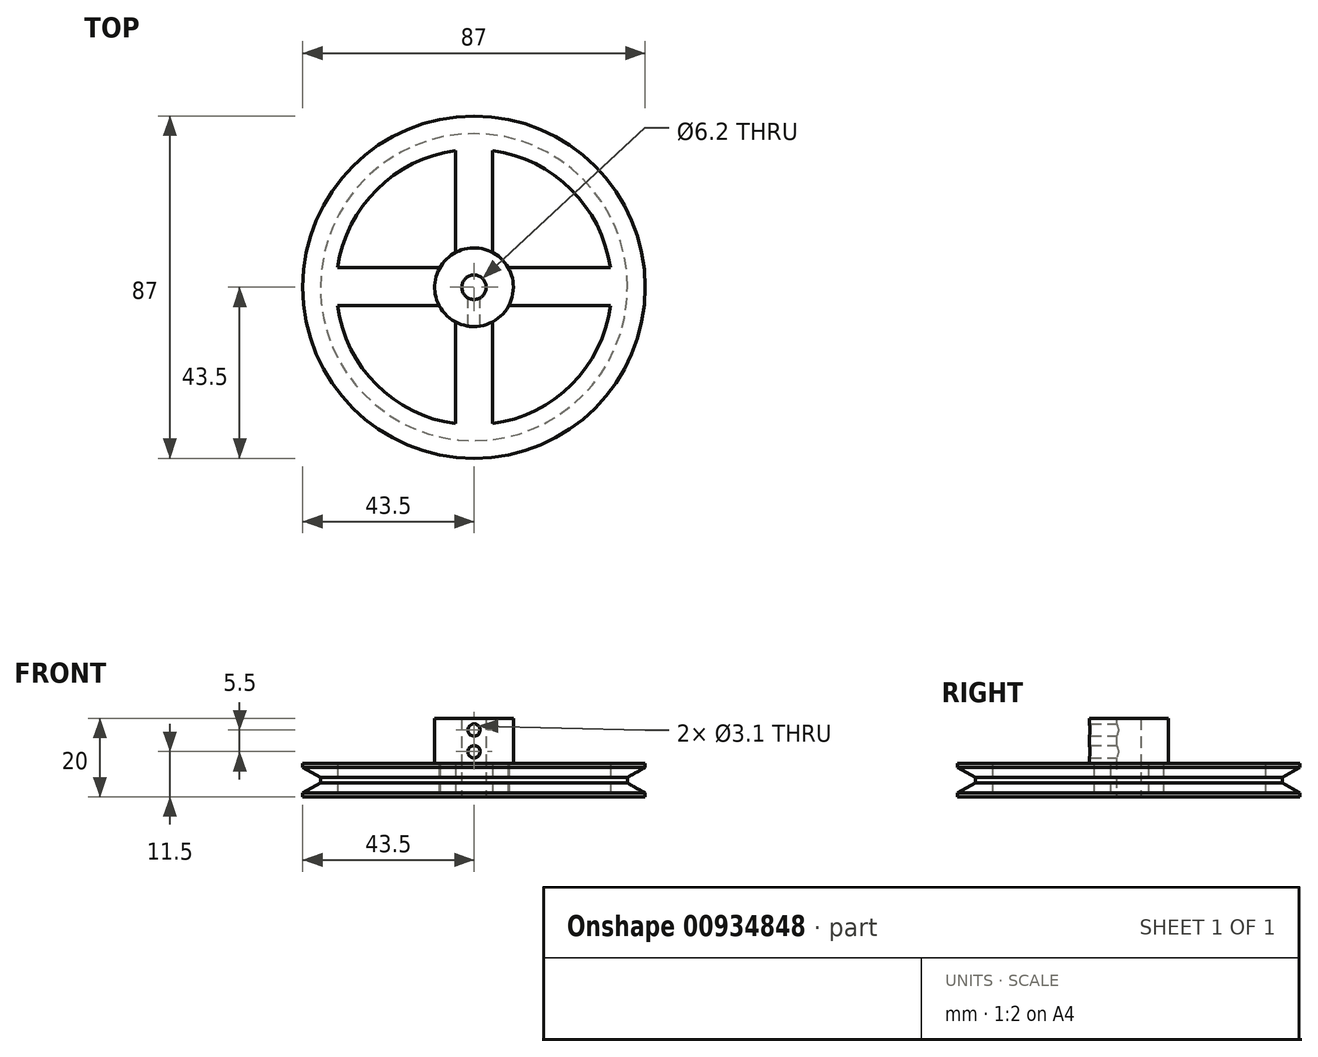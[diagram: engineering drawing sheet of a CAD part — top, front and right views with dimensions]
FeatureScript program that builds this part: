
annotation { "Feature Type Name" : "Feature", "Feature Type Description" : "" }
export const myFeature = defineFeature(function(context is Context, id is Id, definition is map)
    precondition{}
    {
        {
            var Q0;
            Q0=qCreatedBy(makeId("Top.planeOp"),FACE);
            var sketch = newSketch(context, id + "F0", { "sketchPlane" : qUnion([Q0])});
            skCircle(sketch, "E0", {"center": v(0, 0) * mm, "radius": 43.5 * mm});
            skCircle(sketch, "E1", {"center": v(0, 0) * mm, "radius": 39 * mm});
            skCircle(sketch, "E2", {"center": v(0, 0) * mm, "radius": 3.1 * mm});
            skCircle(sketch, "E3", {"center": v(0, 0) * mm, "radius": 10 * mm});
            skLineSegment(sketch, "E4", {"start": v(43.5, 0) * mm, "end": v(-43.5, 0) * mm});
            skLineSegment(sketch, "E5", {"start": v(0, 43.5) * mm, "end": v(0, -43.5) * mm});
            skLineSegment(sketch, "E6", {"start": v(-4.67, -34.69) * mm, "end": v(-4.67, -34.69) * mm});
            skLineSegment(sketch, "E7", {"start": v(4.67, -34.69) * mm, "end": v(4.67, 34.69) * mm});
            skLineSegment(sketch, "E8", {"start": v(34.69, -4.67) * mm, "end": v(-34.69, -4.67) * mm});
            skLineSegment(sketch, "E9", {"start": v(-34.64, 5) * mm, "end": v(-34.64, 5) * mm});
            skLineSegment(sketch, "E10", {"start": v(-4.67, -34.69) * mm, "end": v(-4.67, 34.69) * mm});
            skLineSegment(sketch, "E11", {"start": v(-34.69, -4.67) * mm, "end": v(-34.69, -4.67) * mm});
            skLineSegment(sketch, "E12", {"start": v(-34.64, 5) * mm, "end": v(34.64, 5) * mm});
            skArc(sketch, "E13", {"start": v(-4.67, 34.69) * mm, "mid": v(-24.75, -24.75) * mm, "end": v(34.69, -4.67) * mm});
            skArc(sketch, "E14", {"start": v(4.67, 34.69) * mm, "mid": v(0, 35) * mm, "end": v(-4.67, 34.69) * mm});
            skArc(sketch, "E15", {"start": v(34.64, 5) * mm, "mid": v(24.63, 24.87) * mm, "end": v(4.67, 34.69) * mm});
            skArc(sketch, "E16", {"start": v(34.69, -4.67) * mm, "mid": v(35, 0.17) * mm, "end": v(34.64, 5) * mm});
            skSolve(sketch);
        }
        {
            var Q0;
            Q0 = qSketchRegion(id + "F0", true);
            var Q1;
            Q1=makeQuery(id+"F0.imprint","IMPRINT",FACE,{"disambiguationData":[TD([[makeQuery(id+"F0.imprint","IMPRINT",EDGE,{"derivedFrom":sQuery(id+"F0.wireOp",EDGE,"E1")}),1.0]])]});
            var Q2;
            {var subQ2=sQuery(id+"F0.wireOp",EDGE,"Dt7iSOTS-iNF6-Fj9d-QwL8-E1cNRbcfdXUS");var subQ4=sQuery(id+"F0.wireOp",EDGE,"E1");var subQ5=makeQuery(id+"F0.imprint","INTERSECT",VERTEX,{"disambiguationData":[OD(0.0)],"derivedFrom":[subQ4,subQ2]});Q2=makeQuery(id+"F0.imprint","IMPRINT",FACE,{"disambiguationData":[TD([[makeQuery(id+"F0.imprint","IMPRINT",EDGE,{"disambiguationData":[TD([[subQ5,-1.0]])],"derivedFrom":subQ4}),1.0]])]});}
            var Q3;
            {var subQ4=sQuery(id+"F0.wireOp",EDGE,"E1");var subQ6=sQuery(id+"F0.wireOp",EDGE,"f54aecad-8b98-43cd-b3f4-bd551124e2040.MirrorCS");var subQ7=makeQuery(id+"F0.imprint","INTERSECT",VERTEX,{"disambiguationData":[OD(1.0)],"derivedFrom":[subQ4,subQ6]});Q3=makeQuery(id+"F0.imprint","IMPRINT",FACE,{"disambiguationData":[TD([[makeQuery(id+"F0.imprint","IMPRINT",EDGE,{"disambiguationData":[TD([[subQ7,1.0]])],"derivedFrom":subQ4}),1.0]])]});}
            var Q4;
            {var subQ5=sQuery(id+"F0.wireOp",EDGE,"E3");var subQ7=sQuery(id+"F0.wireOp",EDGE,"E5");var subQ8=makeQuery(id+"F0.imprint","INTERSECT",VERTEX,{"disambiguationData":[OD(1.0)],"derivedFrom":[subQ5,subQ7]});Q4=makeQuery(id+"F0.imprint","IMPRINT",FACE,{"disambiguationData":[TD([[makeQuery(id+"F0.imprint","IMPRINT",EDGE,{"disambiguationData":[TD([[subQ8,-1.0]])],"derivedFrom":subQ5}),-1.0]])]});}
            var Q5;
            {var subQ3=sQuery(id+"F0.wireOp",EDGE,"Dt7iSOTS-iNF6-Fj9d-QwL8-E1cNRbcfdXUS");var subQ5=sQuery(id+"F0.wireOp",EDGE,"E3");var subQ6=makeQuery(id+"F0.imprint","INTERSECT",VERTEX,{"disambiguationData":[OD(1.0)],"derivedFrom":[subQ5,subQ3]});Q5=makeQuery(id+"F0.imprint","IMPRINT",FACE,{"disambiguationData":[TD([[makeQuery(id+"F0.imprint","IMPRINT",EDGE,{"disambiguationData":[TD([[subQ6,-1.0]])],"derivedFrom":subQ5}),-1.0]])]});}
            var Q6;
            {var subQ0=sQuery(id+"F0.wireOp",EDGE,"Dt7iSOTS-iNF6-Fj9d-QwL8-E1cNRbcfdXUS");var subQ1=sQuery(id+"F0.wireOp",EDGE,"E3");var subQ2=makeQuery(id+"F0.imprint","INTERSECT",VERTEX,{"disambiguationData":[OD(1.0)],"derivedFrom":[subQ1,subQ0]});Q6=makeQuery(id+"F0.imprint","IMPRINT",FACE,{"disambiguationData":[TD([[makeQuery(id+"F0.imprint","IMPRINT",EDGE,{"disambiguationData":[TD([[subQ2,-1.0]])],"derivedFrom":subQ1}),1.0]])]});}
            var Q7;
            {var subQ0=sQuery(id+"F0.wireOp",EDGE,"E5");var subQ1=sQuery(id+"F0.wireOp",EDGE,"E3");var subQ2=makeQuery(id+"F0.imprint","INTERSECT",VERTEX,{"disambiguationData":[OD(1.0)],"derivedFrom":[subQ1,subQ0]});Q7=makeQuery(id+"F0.imprint","IMPRINT",FACE,{"disambiguationData":[TD([[makeQuery(id+"F0.imprint","IMPRINT",EDGE,{"disambiguationData":[TD([[subQ2,-1.0]])],"derivedFrom":subQ1}),1.0]])]});}
            var Q8;
            {var subQ0=sQuery(id+"F0.wireOp",EDGE,"E5");var subQ1=sQuery(id+"F0.wireOp",EDGE,"E2");var subQ2=makeQuery(id+"F0.imprint","INTERSECT",VERTEX,{"disambiguationData":[OD(1.0)],"derivedFrom":[subQ1,subQ0]});Q8=makeQuery(id+"F0.imprint","IMPRINT",FACE,{"disambiguationData":[TD([[makeQuery(id+"F0.imprint","IMPRINT",EDGE,{"disambiguationData":[TD([[subQ2,-1.0]])],"derivedFrom":subQ1}),-1.0]])]});}
            var Q9;
            {var subQ0=sQuery(id+"F0.wireOp",EDGE,"Dt7iSOTS-iNF6-Fj9d-QwL8-E1cNRbcfdXUS");var subQ1=sQuery(id+"F0.wireOp",EDGE,"E2");var subQ2=makeQuery(id+"F0.imprint","INTERSECT",VERTEX,{"disambiguationData":[OD(1.0)],"derivedFrom":[subQ1,subQ0]});Q9=makeQuery(id+"F0.imprint","IMPRINT",FACE,{"disambiguationData":[TD([[makeQuery(id+"F0.imprint","IMPRINT",EDGE,{"disambiguationData":[TD([[subQ2,-1.0]])],"derivedFrom":subQ1}),-1.0]])]});}
            var Q10;
            {var subQ0=sQuery(id+"F0.wireOp",EDGE,"E10");var subQ1=sQuery(id+"F0.wireOp",EDGE,"E3");var subQ2=makeQuery(id+"F0.imprint","INTERSECT",VERTEX,{"disambiguationData":[OD(1.0)],"derivedFrom":[subQ1,subQ0]});Q10=makeQuery(id+"F0.imprint","IMPRINT",FACE,{"disambiguationData":[TD([[makeQuery(id+"F0.imprint","IMPRINT",EDGE,{"disambiguationData":[TD([[subQ2,-1.0]])],"derivedFrom":subQ1}),1.0]])]});}
            var Q11;
            {var subQ0=sQuery(id+"F0.wireOp",EDGE,"E10");var subQ1=sQuery(id+"F0.wireOp",EDGE,"E3");var subQ2=makeQuery(id+"F0.imprint","INTERSECT",VERTEX,{"disambiguationData":[OD(1.0)],"derivedFrom":[subQ1,subQ0]});Q11=makeQuery(id+"F0.imprint","IMPRINT",FACE,{"disambiguationData":[TD([[makeQuery(id+"F0.imprint","IMPRINT",EDGE,{"disambiguationData":[TD([[subQ2,-1.0]])],"derivedFrom":subQ1}),-1.0]])]});}
            var Q12;
            {var subQ0=sQuery(id+"F0.wireOp",EDGE,"f54aecad-8b98-43cd-b3f4-bd551124e2040.MirrorCS");var subQ1=sQuery(id+"F0.wireOp",EDGE,"E3");var subQ2=makeQuery(id+"F0.imprint","INTERSECT",VERTEX,{"disambiguationData":[OD(1.0)],"derivedFrom":[subQ1,subQ0]});Q12=makeQuery(id+"F0.imprint","IMPRINT",FACE,{"disambiguationData":[TD([[makeQuery(id+"F0.imprint","IMPRINT",EDGE,{"disambiguationData":[TD([[subQ2,-1.0]])],"derivedFrom":subQ1}),-1.0]])]});}
            var Q13;
            {var subQ0=sQuery(id+"F0.wireOp",EDGE,"f54aecad-8b98-43cd-b3f4-bd551124e2040.MirrorCS");var subQ1=sQuery(id+"F0.wireOp",EDGE,"E3");var subQ2=makeQuery(id+"F0.imprint","INTERSECT",VERTEX,{"disambiguationData":[OD(1.0)],"derivedFrom":[subQ1,subQ0]});Q13=makeQuery(id+"F0.imprint","IMPRINT",FACE,{"disambiguationData":[TD([[makeQuery(id+"F0.imprint","IMPRINT",EDGE,{"disambiguationData":[TD([[subQ2,-1.0]])],"derivedFrom":subQ1}),1.0]])]});}
            var Q14;
            {var subQ0=sQuery(id+"F0.wireOp",EDGE,"f54aecad-8b98-43cd-b3f4-bd551124e2040.MirrorCS");var subQ1=sQuery(id+"F0.wireOp",EDGE,"E2");var subQ2=makeQuery(id+"F0.imprint","INTERSECT",VERTEX,{"disambiguationData":[OD(1.0)],"derivedFrom":[subQ1,subQ0]});Q14=makeQuery(id+"F0.imprint","IMPRINT",FACE,{"disambiguationData":[TD([[makeQuery(id+"F0.imprint","IMPRINT",EDGE,{"disambiguationData":[TD([[subQ2,-1.0]])],"derivedFrom":subQ1}),-1.0]])]});}
            var Q15;
            {var subQ0=sQuery(id+"F0.wireOp",EDGE,"0fc9e538-063d-4069-807a-62193617adc70.MirrorCS");var subQ1=sQuery(id+"F0.wireOp",EDGE,"E2");var subQ2=makeQuery(id+"F0.imprint","INTERSECT",VERTEX,{"disambiguationData":[OD(1.0)],"derivedFrom":[subQ1,subQ0]});Q15=makeQuery(id+"F0.imprint","IMPRINT",FACE,{"disambiguationData":[TD([[makeQuery(id+"F0.imprint","IMPRINT",EDGE,{"disambiguationData":[TD([[subQ2,-1.0]])],"derivedFrom":subQ1}),-1.0]])]});}
            var Q16;
            {var subQ0=sQuery(id+"F0.wireOp",EDGE,"E4");var subQ1=sQuery(id+"F0.wireOp",EDGE,"E2");var subQ2=makeQuery(id+"F0.imprint","INTERSECT",VERTEX,{"disambiguationData":[OD(0.0)],"derivedFrom":[subQ1,subQ0]});Q16=makeQuery(id+"F0.imprint","IMPRINT",FACE,{"disambiguationData":[TD([[makeQuery(id+"F0.imprint","IMPRINT",EDGE,{"disambiguationData":[TD([[subQ2,1.0]])],"derivedFrom":subQ1}),-1.0]])]});}
            var Q17;
            {var subQ0=sQuery(id+"F0.wireOp",EDGE,"c9230b24-fb15-4a67-97de-4f06d66d76500.MirrorCS");var subQ1=sQuery(id+"F0.wireOp",EDGE,"E2");var subQ2=makeQuery(id+"F0.imprint","INTERSECT",VERTEX,{"disambiguationData":[OD(0.0)],"derivedFrom":[subQ1,subQ0]});Q17=makeQuery(id+"F0.imprint","IMPRINT",FACE,{"disambiguationData":[TD([[makeQuery(id+"F0.imprint","IMPRINT",EDGE,{"disambiguationData":[TD([[subQ2,1.0]])],"derivedFrom":subQ1}),-1.0]])]});}
            var Q18;
            {var subQ0=sQuery(id+"F0.wireOp",EDGE,"c9230b24-fb15-4a67-97de-4f06d66d76500.MirrorCS");var subQ1=sQuery(id+"F0.wireOp",EDGE,"E2");var subQ2=makeQuery(id+"F0.imprint","INTERSECT",VERTEX,{"disambiguationData":[OD(0.0)],"derivedFrom":[subQ1,subQ0]});Q18=makeQuery(id+"F0.imprint","IMPRINT",FACE,{"disambiguationData":[TD([[makeQuery(id+"F0.imprint","IMPRINT",EDGE,{"disambiguationData":[TD([[subQ2,-1.0]])],"derivedFrom":subQ1}),-1.0]])]});}
            var Q19;
            {var subQ0=sQuery(id+"F0.wireOp",EDGE,"X2wNwJQT-B4Tv-bB2O-wKaQ-eUmFgRdWR0iJ");var subQ1=sQuery(id+"F0.wireOp",EDGE,"E2");var subQ2=makeQuery(id+"F0.imprint","INTERSECT",VERTEX,{"disambiguationData":[OD(0.0)],"derivedFrom":[subQ1,subQ0]});Q19=makeQuery(id+"F0.imprint","IMPRINT",FACE,{"disambiguationData":[TD([[makeQuery(id+"F0.imprint","IMPRINT",EDGE,{"disambiguationData":[TD([[subQ2,-1.0]])],"derivedFrom":subQ1}),-1.0]])]});}
            var Q20;
            {var subQ0=sQuery(id+"F0.wireOp",EDGE,"Dt7iSOTS-iNF6-Fj9d-QwL8-E1cNRbcfdXUS");var subQ1=sQuery(id+"F0.wireOp",EDGE,"E2");var subQ2=makeQuery(id+"F0.imprint","INTERSECT",VERTEX,{"disambiguationData":[OD(0.0)],"derivedFrom":[subQ1,subQ0]});Q20=makeQuery(id+"F0.imprint","IMPRINT",FACE,{"disambiguationData":[TD([[makeQuery(id+"F0.imprint","IMPRINT",EDGE,{"disambiguationData":[TD([[subQ2,-1.0]])],"derivedFrom":subQ1}),-1.0]])]});}
            var Q21;
            {var subQ0=sQuery(id+"F0.wireOp",EDGE,"E5");var subQ1=sQuery(id+"F0.wireOp",EDGE,"E2");var subQ2=makeQuery(id+"F0.imprint","INTERSECT",VERTEX,{"disambiguationData":[OD(0.0)],"derivedFrom":[subQ1,subQ0]});Q21=makeQuery(id+"F0.imprint","IMPRINT",FACE,{"disambiguationData":[TD([[makeQuery(id+"F0.imprint","IMPRINT",EDGE,{"disambiguationData":[TD([[subQ2,-1.0]])],"derivedFrom":subQ1}),-1.0]])]});}
            var Q22;
            {var subQ0=sQuery(id+"F0.wireOp",EDGE,"f54aecad-8b98-43cd-b3f4-bd551124e2040.MirrorCS");var subQ1=sQuery(id+"F0.wireOp",EDGE,"E2");var subQ2=makeQuery(id+"F0.imprint","INTERSECT",VERTEX,{"disambiguationData":[OD(0.0)],"derivedFrom":[subQ1,subQ0]});Q22=makeQuery(id+"F0.imprint","IMPRINT",FACE,{"disambiguationData":[TD([[makeQuery(id+"F0.imprint","IMPRINT",EDGE,{"disambiguationData":[TD([[subQ2,-1.0]])],"derivedFrom":subQ1}),-1.0]])]});}
            var Q23;
            {var subQ0=sQuery(id+"F0.wireOp",EDGE,"0fc9e538-063d-4069-807a-62193617adc70.MirrorCS");var subQ1=sQuery(id+"F0.wireOp",EDGE,"E2");var subQ2=makeQuery(id+"F0.imprint","INTERSECT",VERTEX,{"disambiguationData":[OD(0.0)],"derivedFrom":[subQ1,subQ0]});Q23=makeQuery(id+"F0.imprint","IMPRINT",FACE,{"disambiguationData":[TD([[makeQuery(id+"F0.imprint","IMPRINT",EDGE,{"disambiguationData":[TD([[subQ2,-1.0]])],"derivedFrom":subQ1}),-1.0]])]});}
            var Q24;
            {var subQ0=sQuery(id+"F0.wireOp",EDGE,"f54aecad-8b98-43cd-b3f4-bd551124e2040.MirrorCS");var subQ1=sQuery(id+"F0.wireOp",EDGE,"E3");var subQ2=makeQuery(id+"F0.imprint","INTERSECT",VERTEX,{"disambiguationData":[OD(0.0)],"derivedFrom":[subQ1,subQ0]});Q24=makeQuery(id+"F0.imprint","IMPRINT",FACE,{"disambiguationData":[TD([[makeQuery(id+"F0.imprint","IMPRINT",EDGE,{"disambiguationData":[TD([[subQ2,-1.0]])],"derivedFrom":subQ1}),1.0]])]});}
            var Q25;
            {var subQ0=sQuery(id+"F0.wireOp",EDGE,"E5");var subQ1=sQuery(id+"F0.wireOp",EDGE,"E3");var subQ2=makeQuery(id+"F0.imprint","INTERSECT",VERTEX,{"disambiguationData":[OD(0.0)],"derivedFrom":[subQ1,subQ0]});Q25=makeQuery(id+"F0.imprint","IMPRINT",FACE,{"disambiguationData":[TD([[makeQuery(id+"F0.imprint","IMPRINT",EDGE,{"disambiguationData":[TD([[subQ2,-1.0]])],"derivedFrom":subQ1}),1.0]])]});}
            var Q26;
            {var subQ0=sQuery(id+"F0.wireOp",EDGE,"Dt7iSOTS-iNF6-Fj9d-QwL8-E1cNRbcfdXUS");var subQ1=sQuery(id+"F0.wireOp",EDGE,"E3");var subQ2=makeQuery(id+"F0.imprint","INTERSECT",VERTEX,{"disambiguationData":[OD(0.0)],"derivedFrom":[subQ1,subQ0]});Q26=makeQuery(id+"F0.imprint","IMPRINT",FACE,{"disambiguationData":[TD([[makeQuery(id+"F0.imprint","IMPRINT",EDGE,{"disambiguationData":[TD([[subQ2,-1.0]])],"derivedFrom":subQ1}),1.0]])]});}
            var Q27;
            {var subQ0=sQuery(id+"F0.wireOp",EDGE,"E7");var subQ1=sQuery(id+"F0.wireOp",EDGE,"E3");var subQ2=makeQuery(id+"F0.imprint","INTERSECT",VERTEX,{"disambiguationData":[OD(0.0)],"derivedFrom":[subQ1,subQ0]});Q27=makeQuery(id+"F0.imprint","IMPRINT",FACE,{"disambiguationData":[TD([[makeQuery(id+"F0.imprint","IMPRINT",EDGE,{"disambiguationData":[TD([[subQ2,-1.0]])],"derivedFrom":subQ1}),1.0]])]});}
            var Q28;
            {var subQ0=sQuery(id+"F0.wireOp",EDGE,"X2wNwJQT-B4Tv-bB2O-wKaQ-eUmFgRdWR0iJ");var subQ1=sQuery(id+"F0.wireOp",EDGE,"E2");var subQ2=makeQuery(id+"F0.imprint","INTERSECT",VERTEX,{"disambiguationData":[OD(1.0)],"derivedFrom":[subQ1,subQ0]});Q28=makeQuery(id+"F0.imprint","IMPRINT",FACE,{"disambiguationData":[TD([[makeQuery(id+"F0.imprint","IMPRINT",EDGE,{"disambiguationData":[TD([[subQ2,-1.0]])],"derivedFrom":subQ1}),-1.0]])]});}
            var Q29;
            {var subQ0=sQuery(id+"F0.wireOp",EDGE,"c9230b24-fb15-4a67-97de-4f06d66d76500.MirrorCS");var subQ1=sQuery(id+"F0.wireOp",EDGE,"E2");var subQ2=makeQuery(id+"F0.imprint","INTERSECT",VERTEX,{"disambiguationData":[OD(1.0)],"derivedFrom":[subQ1,subQ0]});Q29=makeQuery(id+"F0.imprint","IMPRINT",FACE,{"disambiguationData":[TD([[makeQuery(id+"F0.imprint","IMPRINT",EDGE,{"disambiguationData":[TD([[subQ2,-1.0]])],"derivedFrom":subQ1}),-1.0]])]});}
            var Q30;
            {var subQ0=sQuery(id+"F0.wireOp",EDGE,"E4");var subQ1=sQuery(id+"F0.wireOp",EDGE,"E2");var subQ2=makeQuery(id+"F0.imprint","INTERSECT",VERTEX,{"disambiguationData":[OD(1.0)],"derivedFrom":[subQ1,subQ0]});Q30=makeQuery(id+"F0.imprint","IMPRINT",FACE,{"disambiguationData":[TD([[makeQuery(id+"F0.imprint","IMPRINT",EDGE,{"disambiguationData":[TD([[subQ2,-1.0]])],"derivedFrom":subQ1}),-1.0]])]});}
            var Q31;
            {var subQ0=sQuery(id+"F0.wireOp",EDGE,"f3349a83-585f-44af-833f-62577e2a71c40.MirrorCS");var subQ1=sQuery(id+"F0.wireOp",EDGE,"E2");var subQ2=makeQuery(id+"F0.imprint","INTERSECT",VERTEX,{"disambiguationData":[OD(0.0)],"derivedFrom":[subQ1,subQ0]});Q31=makeQuery(id+"F0.imprint","IMPRINT",FACE,{"disambiguationData":[TD([[makeQuery(id+"F0.imprint","IMPRINT",EDGE,{"disambiguationData":[TD([[subQ2,-1.0]])],"derivedFrom":subQ1}),-1.0]])]});}
            var Q32;
            {var subQ5=sQuery(id+"F0.wireOp",EDGE,"E3");var subQ7=sQuery(id+"F0.wireOp",EDGE,"E5");var subQ8=makeQuery(id+"F0.imprint","INTERSECT",VERTEX,{"disambiguationData":[OD(0.0)],"derivedFrom":[subQ5,subQ7]});Q32=makeQuery(id+"F0.imprint","IMPRINT",FACE,{"disambiguationData":[TD([[makeQuery(id+"F0.imprint","IMPRINT",EDGE,{"disambiguationData":[TD([[subQ8,-1.0]])],"derivedFrom":subQ5}),-1.0]])]});}
            var Q33;
            {var subQ0=sQuery(id+"F0.wireOp",EDGE,"f54aecad-8b98-43cd-b3f4-bd551124e2040.MirrorCS");var subQ1=sQuery(id+"F0.wireOp",EDGE,"E3");var subQ2=makeQuery(id+"F0.imprint","INTERSECT",VERTEX,{"disambiguationData":[OD(0.0)],"derivedFrom":[subQ1,subQ0]});Q33=makeQuery(id+"F0.imprint","IMPRINT",FACE,{"disambiguationData":[TD([[makeQuery(id+"F0.imprint","IMPRINT",EDGE,{"disambiguationData":[TD([[subQ2,-1.0]])],"derivedFrom":subQ1}),-1.0]])]});}
            var Q34;
            {var subQ0=sQuery(id+"F0.wireOp",EDGE,"E7");var subQ1=sQuery(id+"F0.wireOp",EDGE,"E3");var subQ2=makeQuery(id+"F0.imprint","INTERSECT",VERTEX,{"disambiguationData":[OD(0.0)],"derivedFrom":[subQ1,subQ0]});Q34=makeQuery(id+"F0.imprint","IMPRINT",FACE,{"disambiguationData":[TD([[makeQuery(id+"F0.imprint","IMPRINT",EDGE,{"disambiguationData":[TD([[subQ2,-1.0]])],"derivedFrom":subQ1}),-1.0]])]});}
            var Q35;
            {var subQ0=sQuery(id+"F0.wireOp",EDGE,"Dt7iSOTS-iNF6-Fj9d-QwL8-E1cNRbcfdXUS");var subQ1=sQuery(id+"F0.wireOp",EDGE,"E3");var subQ2=makeQuery(id+"F0.imprint","INTERSECT",VERTEX,{"disambiguationData":[OD(0.0)],"derivedFrom":[subQ1,subQ0]});Q35=makeQuery(id+"F0.imprint","IMPRINT",FACE,{"disambiguationData":[TD([[makeQuery(id+"F0.imprint","IMPRINT",EDGE,{"disambiguationData":[TD([[subQ2,-1.0]])],"derivedFrom":subQ1}),-1.0]])]});}
            var Q36;
            {var subQ0=sQuery(id+"F0.wireOp",EDGE,"Dt7iSOTS-iNF6-Fj9d-QwL8-E1cNRbcfdXUS");var subQ1=sQuery(id+"F0.wireOp",EDGE,"E1");var subQ2=makeQuery(id+"F0.imprint","INTERSECT",VERTEX,{"disambiguationData":[OD(1.0)],"derivedFrom":[subQ1,subQ0]});Q36=makeQuery(id+"F0.imprint","IMPRINT",FACE,{"disambiguationData":[TD([[makeQuery(id+"F0.imprint","IMPRINT",EDGE,{"disambiguationData":[TD([[subQ2,-1.0]])],"derivedFrom":subQ1}),1.0]])]});}
            var Q37;
            {var subQ3=sQuery(id+"F0.wireOp",EDGE,"f54aecad-8b98-43cd-b3f4-bd551124e2040.MirrorCS");var subQ5=sQuery(id+"F0.wireOp",EDGE,"E1");var subQ6=makeQuery(id+"F0.imprint","INTERSECT",VERTEX,{"disambiguationData":[OD(0.0)],"derivedFrom":[subQ5,subQ3]});Q37=makeQuery(id+"F0.imprint","IMPRINT",FACE,{"disambiguationData":[TD([[makeQuery(id+"F0.imprint","IMPRINT",EDGE,{"disambiguationData":[TD([[subQ6,1.0]])],"derivedFrom":subQ5}),1.0]])]});}
            var Q38;
            {var subQ2=sQuery(id+"F0.wireOp",EDGE,"f3349a83-585f-44af-833f-62577e2a71c40.MirrorCS");var subQ4=sQuery(id+"F0.wireOp",EDGE,"E1");var subQ5=makeQuery(id+"F0.imprint","INTERSECT",VERTEX,{"disambiguationData":[OD(0.0)],"derivedFrom":[subQ4,subQ2]});Q38=makeQuery(id+"F0.imprint","IMPRINT",FACE,{"disambiguationData":[TD([[makeQuery(id+"F0.imprint","IMPRINT",EDGE,{"disambiguationData":[TD([[subQ5,-1.0]])],"derivedFrom":subQ4}),1.0]])]});}
            var Q39;
            {var subQ0=sQuery(id+"F0.wireOp",EDGE,"c9230b24-fb15-4a67-97de-4f06d66d76500.MirrorCS");var subQ1=sQuery(id+"F0.wireOp",EDGE,"E1");var subQ2=makeQuery(id+"F0.imprint","INTERSECT",VERTEX,{"disambiguationData":[OD(0.0)],"derivedFrom":[subQ1,subQ0]});Q39=makeQuery(id+"F0.imprint","IMPRINT",FACE,{"disambiguationData":[TD([[makeQuery(id+"F0.imprint","IMPRINT",EDGE,{"disambiguationData":[TD([[subQ2,1.0]])],"derivedFrom":subQ1}),1.0]])]});}
            var Q40;
            {var subQ0=sQuery(id+"F0.wireOp",EDGE,"f3349a83-585f-44af-833f-62577e2a71c40.MirrorCS");var subQ1=sQuery(id+"F0.wireOp",EDGE,"E3");var subQ2=makeQuery(id+"F0.imprint","INTERSECT",VERTEX,{"disambiguationData":[OD(0.0)],"derivedFrom":[subQ1,subQ0]});Q40=makeQuery(id+"F0.imprint","IMPRINT",FACE,{"disambiguationData":[TD([[makeQuery(id+"F0.imprint","IMPRINT",EDGE,{"disambiguationData":[TD([[subQ2,-1.0]])],"derivedFrom":subQ1}),1.0]])]});}
            var Q41;
            {var subQ0=sQuery(id+"F0.wireOp",EDGE,"E4");var subQ1=sQuery(id+"F0.wireOp",EDGE,"E3");var subQ2=makeQuery(id+"F0.imprint","INTERSECT",VERTEX,{"disambiguationData":[OD(1.0)],"derivedFrom":[subQ1,subQ0]});Q41=makeQuery(id+"F0.imprint","IMPRINT",FACE,{"disambiguationData":[TD([[makeQuery(id+"F0.imprint","IMPRINT",EDGE,{"disambiguationData":[TD([[subQ2,-1.0]])],"derivedFrom":subQ1}),1.0]])]});}
            var Q42;
            {var subQ0=sQuery(id+"F0.wireOp",EDGE,"c9230b24-fb15-4a67-97de-4f06d66d76500.MirrorCS");var subQ1=sQuery(id+"F0.wireOp",EDGE,"E3");var subQ2=makeQuery(id+"F0.imprint","INTERSECT",VERTEX,{"disambiguationData":[OD(1.0)],"derivedFrom":[subQ1,subQ0]});Q42=makeQuery(id+"F0.imprint","IMPRINT",FACE,{"disambiguationData":[TD([[makeQuery(id+"F0.imprint","IMPRINT",EDGE,{"disambiguationData":[TD([[subQ2,-1.0]])],"derivedFrom":subQ1}),1.0]])]});}
            var Q43;
            {var subQ0=sQuery(id+"F0.wireOp",EDGE,"c9230b24-fb15-4a67-97de-4f06d66d76500.MirrorCS");var subQ1=sQuery(id+"F0.wireOp",EDGE,"E3");var subQ2=makeQuery(id+"F0.imprint","INTERSECT",VERTEX,{"disambiguationData":[OD(1.0)],"derivedFrom":[subQ1,subQ0]});Q43=makeQuery(id+"F0.imprint","IMPRINT",FACE,{"disambiguationData":[TD([[makeQuery(id+"F0.imprint","IMPRINT",EDGE,{"disambiguationData":[TD([[subQ2,-1.0]])],"derivedFrom":subQ1}),-1.0]])]});}
            var Q44;
            {var subQ5=sQuery(id+"F0.wireOp",EDGE,"E3");var subQ7=sQuery(id+"F0.wireOp",EDGE,"E4");var subQ8=makeQuery(id+"F0.imprint","INTERSECT",VERTEX,{"disambiguationData":[OD(1.0)],"derivedFrom":[subQ5,subQ7]});Q44=makeQuery(id+"F0.imprint","IMPRINT",FACE,{"disambiguationData":[TD([[makeQuery(id+"F0.imprint","IMPRINT",EDGE,{"disambiguationData":[TD([[subQ8,-1.0]])],"derivedFrom":subQ5}),-1.0]])]});}
            var Q45;
            {var subQ1=sQuery(id+"F0.wireOp",EDGE,"E3");var subQ5=sQuery(id+"F0.wireOp",EDGE,"f3349a83-585f-44af-833f-62577e2a71c40.MirrorCS");var subQ6=makeQuery(id+"F0.imprint","INTERSECT",VERTEX,{"disambiguationData":[OD(0.0)],"derivedFrom":[subQ1,subQ5]});Q45=makeQuery(id+"F0.imprint","IMPRINT",FACE,{"disambiguationData":[TD([[makeQuery(id+"F0.imprint","IMPRINT",EDGE,{"disambiguationData":[TD([[subQ6,-1.0]])],"derivedFrom":subQ1}),-1.0]])]});}
            var Q46;
            {var subQ0=sQuery(id+"F0.wireOp",EDGE,"E12");var subQ1=sQuery(id+"F0.wireOp",EDGE,"E3");var subQ2=makeQuery(id+"F0.imprint","INTERSECT",VERTEX,{"disambiguationData":[OD(1.0)],"derivedFrom":[subQ1,subQ0]});Q46=makeQuery(id+"F0.imprint","IMPRINT",FACE,{"disambiguationData":[TD([[makeQuery(id+"F0.imprint","IMPRINT",EDGE,{"disambiguationData":[TD([[subQ2,-1.0]])],"derivedFrom":subQ1}),-1.0]])]});}
            var Q47;
            {var subQ0=sQuery(id+"F0.wireOp",EDGE,"E12");var subQ1=sQuery(id+"F0.wireOp",EDGE,"E3");var subQ2=makeQuery(id+"F0.imprint","INTERSECT",VERTEX,{"disambiguationData":[OD(1.0)],"derivedFrom":[subQ1,subQ0]});Q47=makeQuery(id+"F0.imprint","IMPRINT",FACE,{"disambiguationData":[TD([[makeQuery(id+"F0.imprint","IMPRINT",EDGE,{"disambiguationData":[TD([[subQ2,-1.0]])],"derivedFrom":subQ1}),1.0]])]});}
            var Q48;
            {var subQ3=sQuery(id+"F0.wireOp",EDGE,"f3349a83-585f-44af-833f-62577e2a71c40.MirrorCS");var subQ5=sQuery(id+"F0.wireOp",EDGE,"E1");var subQ6=makeQuery(id+"F0.imprint","INTERSECT",VERTEX,{"disambiguationData":[OD(1.0)],"derivedFrom":[subQ5,subQ3]});Q48=makeQuery(id+"F0.imprint","IMPRINT",FACE,{"disambiguationData":[TD([[makeQuery(id+"F0.imprint","IMPRINT",EDGE,{"disambiguationData":[TD([[subQ6,-1.0]])],"derivedFrom":subQ5}),1.0]])]});}
            var Q49;
            {var subQ3=sQuery(id+"F0.wireOp",EDGE,"c9230b24-fb15-4a67-97de-4f06d66d76500.MirrorCS");var subQ6=sQuery(id+"F0.wireOp",EDGE,"E1");var subQ9=makeQuery(id+"F0.imprint","INTERSECT",VERTEX,{"disambiguationData":[OD(1.0)],"derivedFrom":[subQ6,subQ3]});Q49=makeQuery(id+"F0.imprint","IMPRINT",FACE,{"disambiguationData":[TD([[makeQuery(id+"F0.imprint","IMPRINT",EDGE,{"disambiguationData":[TD([[subQ9,1.0]])],"derivedFrom":subQ6}),1.0]])]});}
            var Q50;
            {var subQ0=sQuery(id+"F0.wireOp",EDGE,"c9230b24-fb15-4a67-97de-4f06d66d76500.MirrorCS");var subQ1=sQuery(id+"F0.wireOp",EDGE,"E3");var subQ2=makeQuery(id+"F0.imprint","INTERSECT",VERTEX,{"disambiguationData":[OD(0.0)],"derivedFrom":[subQ1,subQ0]});Q50=makeQuery(id+"F0.imprint","IMPRINT",FACE,{"disambiguationData":[TD([[makeQuery(id+"F0.imprint","IMPRINT",EDGE,{"disambiguationData":[TD([[subQ2,1.0]])],"derivedFrom":subQ1}),-1.0]])]});}
            var Q51;
            {var subQ5=sQuery(id+"F0.wireOp",EDGE,"E4");var subQ6=sQuery(id+"F0.wireOp",EDGE,"E3");var subQ7=makeQuery(id+"F0.imprint","INTERSECT",VERTEX,{"disambiguationData":[OD(0.0)],"derivedFrom":[subQ6,subQ5]});Q51=makeQuery(id+"F0.imprint","IMPRINT",FACE,{"disambiguationData":[TD([[makeQuery(id+"F0.imprint","IMPRINT",EDGE,{"disambiguationData":[TD([[subQ7,1.0]])],"derivedFrom":subQ6}),-1.0]])]});}
            var Q52;
            {var subQ0=sQuery(id+"F0.wireOp",EDGE,"E8");var subQ1=sQuery(id+"F0.wireOp",EDGE,"E3");var subQ2=makeQuery(id+"F0.imprint","INTERSECT",VERTEX,{"disambiguationData":[OD(1.0)],"derivedFrom":[subQ1,subQ0]});Q52=makeQuery(id+"F0.imprint","IMPRINT",FACE,{"disambiguationData":[TD([[makeQuery(id+"F0.imprint","IMPRINT",EDGE,{"disambiguationData":[TD([[subQ2,-1.0]])],"derivedFrom":subQ1}),1.0]])]});}
            var Q53;
            {var subQ0=sQuery(id+"F0.wireOp",EDGE,"E8");var subQ1=sQuery(id+"F0.wireOp",EDGE,"E3");var subQ2=makeQuery(id+"F0.imprint","INTERSECT",VERTEX,{"disambiguationData":[OD(1.0)],"derivedFrom":[subQ1,subQ0]});Q53=makeQuery(id+"F0.imprint","IMPRINT",FACE,{"disambiguationData":[TD([[makeQuery(id+"F0.imprint","IMPRINT",EDGE,{"disambiguationData":[TD([[subQ2,-1.0]])],"derivedFrom":subQ1}),-1.0]])]});}
            var Q54;
            {var subQ0=sQuery(id+"F0.wireOp",EDGE,"E4");var subQ1=sQuery(id+"F0.wireOp",EDGE,"E3");var subQ2=makeQuery(id+"F0.imprint","INTERSECT",VERTEX,{"disambiguationData":[OD(0.0)],"derivedFrom":[subQ1,subQ0]});Q54=makeQuery(id+"F0.imprint","IMPRINT",FACE,{"disambiguationData":[TD([[makeQuery(id+"F0.imprint","IMPRINT",EDGE,{"disambiguationData":[TD([[subQ2,1.0]])],"derivedFrom":subQ1}),1.0]])]});}
            var Q55;
            {var subQ0=sQuery(id+"F0.wireOp",EDGE,"c9230b24-fb15-4a67-97de-4f06d66d76500.MirrorCS");var subQ1=sQuery(id+"F0.wireOp",EDGE,"E3");var subQ2=makeQuery(id+"F0.imprint","INTERSECT",VERTEX,{"disambiguationData":[OD(0.0)],"derivedFrom":[subQ1,subQ0]});Q55=makeQuery(id+"F0.imprint","IMPRINT",FACE,{"disambiguationData":[TD([[makeQuery(id+"F0.imprint","IMPRINT",EDGE,{"disambiguationData":[TD([[subQ2,1.0]])],"derivedFrom":subQ1}),1.0]])]});}
            var Q56;
            {var subQ0=sQuery(id+"F0.wireOp",EDGE,"c9230b24-fb15-4a67-97de-4f06d66d76500.MirrorCS");var subQ1=sQuery(id+"F0.wireOp",EDGE,"E3");var subQ2=makeQuery(id+"F0.imprint","INTERSECT",VERTEX,{"disambiguationData":[OD(0.0)],"derivedFrom":[subQ1,subQ0]});Q56=makeQuery(id+"F0.imprint","IMPRINT",FACE,{"disambiguationData":[TD([[makeQuery(id+"F0.imprint","IMPRINT",EDGE,{"disambiguationData":[TD([[subQ2,-1.0]])],"derivedFrom":subQ1}),1.0]])]});}
            var Q57;
            {var subQ0=sQuery(id+"F0.wireOp",EDGE,"c9230b24-fb15-4a67-97de-4f06d66d76500.MirrorCS");var subQ1=sQuery(id+"F0.wireOp",EDGE,"E3");var subQ2=makeQuery(id+"F0.imprint","INTERSECT",VERTEX,{"disambiguationData":[OD(0.0)],"derivedFrom":[subQ1,subQ0]});Q57=makeQuery(id+"F0.imprint","IMPRINT",FACE,{"disambiguationData":[TD([[makeQuery(id+"F0.imprint","IMPRINT",EDGE,{"disambiguationData":[TD([[subQ2,-1.0]])],"derivedFrom":subQ1}),-1.0]])]});}
            var Q58;
            {var subQ0=sQuery(id+"F0.wireOp",EDGE,"E7");var subQ1=sQuery(id+"F0.wireOp",EDGE,"E3");var subQ2=makeQuery(id+"F0.imprint","INTERSECT",VERTEX,{"disambiguationData":[OD(1.0)],"derivedFrom":[subQ1,subQ0]});Q58=makeQuery(id+"F0.imprint","IMPRINT",FACE,{"disambiguationData":[TD([[makeQuery(id+"F0.imprint","IMPRINT",EDGE,{"disambiguationData":[TD([[subQ2,-1.0]])],"derivedFrom":subQ1}),1.0]])]});}
            var Q59;
            {var subQ0=sQuery(id+"F0.wireOp",EDGE,"0fc9e538-063d-4069-807a-62193617adc70.MirrorCS");var subQ1=sQuery(id+"F0.wireOp",EDGE,"E3");var subQ2=makeQuery(id+"F0.imprint","INTERSECT",VERTEX,{"disambiguationData":[OD(1.0)],"derivedFrom":[subQ1,subQ0]});Q59=makeQuery(id+"F0.imprint","IMPRINT",FACE,{"disambiguationData":[TD([[makeQuery(id+"F0.imprint","IMPRINT",EDGE,{"disambiguationData":[TD([[subQ2,-1.0]])],"derivedFrom":subQ1}),1.0]])]});}
            var Q60;
            {var subQ0=sQuery(id+"F0.wireOp",EDGE,"E12");var subQ1=sQuery(id+"F0.wireOp",EDGE,"E3");var subQ2=makeQuery(id+"F0.imprint","INTERSECT",VERTEX,{"disambiguationData":[OD(0.0)],"derivedFrom":[subQ1,subQ0]});Q60=makeQuery(id+"F0.imprint","IMPRINT",FACE,{"disambiguationData":[TD([[makeQuery(id+"F0.imprint","IMPRINT",EDGE,{"disambiguationData":[TD([[subQ2,-1.0]])],"derivedFrom":subQ1}),1.0]])]});}
            var Q61;
            {var subQ0=sQuery(id+"F0.wireOp",EDGE,"X2wNwJQT-B4Tv-bB2O-wKaQ-eUmFgRdWR0iJ");var subQ1=sQuery(id+"F0.wireOp",EDGE,"E3");var subQ2=makeQuery(id+"F0.imprint","INTERSECT",VERTEX,{"disambiguationData":[OD(0.0)],"derivedFrom":[subQ1,subQ0]});Q61=makeQuery(id+"F0.imprint","IMPRINT",FACE,{"disambiguationData":[TD([[makeQuery(id+"F0.imprint","IMPRINT",EDGE,{"disambiguationData":[TD([[subQ2,-1.0]])],"derivedFrom":subQ1}),1.0]])]});}
            var Q62;
            {var subQ0=sQuery(id+"F0.wireOp",EDGE,"0fc9e538-063d-4069-807a-62193617adc70.MirrorCS");var subQ1=sQuery(id+"F0.wireOp",EDGE,"E3");var subQ2=makeQuery(id+"F0.imprint","INTERSECT",VERTEX,{"disambiguationData":[OD(0.0)],"derivedFrom":[subQ1,subQ0]});Q62=makeQuery(id+"F0.imprint","IMPRINT",FACE,{"disambiguationData":[TD([[makeQuery(id+"F0.imprint","IMPRINT",EDGE,{"disambiguationData":[TD([[subQ2,-1.0]])],"derivedFrom":subQ1}),1.0]])]});}
            var Q63;
            {var subQ0=sQuery(id+"F0.wireOp",EDGE,"E10");var subQ1=sQuery(id+"F0.wireOp",EDGE,"E3");var subQ2=makeQuery(id+"F0.imprint","INTERSECT",VERTEX,{"disambiguationData":[OD(0.0)],"derivedFrom":[subQ1,subQ0]});Q63=makeQuery(id+"F0.imprint","IMPRINT",FACE,{"disambiguationData":[TD([[makeQuery(id+"F0.imprint","IMPRINT",EDGE,{"disambiguationData":[TD([[subQ2,-1.0]])],"derivedFrom":subQ1}),1.0]])]});}
            var Q64;
            {var subQ0=sQuery(id+"F0.wireOp",EDGE,"X2wNwJQT-B4Tv-bB2O-wKaQ-eUmFgRdWR0iJ");var subQ1=sQuery(id+"F0.wireOp",EDGE,"E3");var subQ2=makeQuery(id+"F0.imprint","INTERSECT",VERTEX,{"disambiguationData":[OD(1.0)],"derivedFrom":[subQ1,subQ0]});Q64=makeQuery(id+"F0.imprint","IMPRINT",FACE,{"disambiguationData":[TD([[makeQuery(id+"F0.imprint","IMPRINT",EDGE,{"disambiguationData":[TD([[subQ2,-1.0]])],"derivedFrom":subQ1}),1.0]])]});}
            var Q65;
            {var subQ0=sQuery(id+"F0.wireOp",EDGE,"E8");var subQ1=sQuery(id+"F0.wireOp",EDGE,"E3");var subQ2=makeQuery(id+"F0.imprint","INTERSECT",VERTEX,{"disambiguationData":[OD(0.0)],"derivedFrom":[subQ1,subQ0]});Q65=makeQuery(id+"F0.imprint","IMPRINT",FACE,{"disambiguationData":[TD([[makeQuery(id+"F0.imprint","IMPRINT",EDGE,{"disambiguationData":[TD([[subQ2,-1.0]])],"derivedFrom":subQ1}),1.0]])]});}
            var Q66;
            {var subQ0=sQuery(id+"F0.wireOp",EDGE,"E12");var subQ1=sQuery(id+"F0.wireOp",EDGE,"E3");var subQ2=makeQuery(id+"F0.imprint","INTERSECT",VERTEX,{"disambiguationData":[OD(0.0)],"derivedFrom":[subQ1,subQ0]});Q66=makeQuery(id+"F0.imprint","IMPRINT",FACE,{"disambiguationData":[TD([[makeQuery(id+"F0.imprint","IMPRINT",EDGE,{"disambiguationData":[TD([[subQ2,1.0]])],"derivedFrom":subQ1}),1.0]])]});}
            var Q67;
            {var subQ0=sQuery(id+"F0.wireOp",EDGE,"E12");var subQ1=sQuery(id+"F0.wireOp",EDGE,"E3");var subQ2=makeQuery(id+"F0.imprint","INTERSECT",VERTEX,{"disambiguationData":[OD(0.0)],"derivedFrom":[subQ1,subQ0]});Q67=makeQuery(id+"F0.imprint","IMPRINT",FACE,{"disambiguationData":[TD([[makeQuery(id+"F0.imprint","IMPRINT",EDGE,{"disambiguationData":[TD([[subQ2,1.0]])],"derivedFrom":subQ1}),-1.0]])]});}
            var Q68;
            {var subQ5=sQuery(id+"F0.wireOp",EDGE,"E5");var subQ6=sQuery(id+"F0.wireOp",EDGE,"E2");var subQ7=makeQuery(id+"F0.imprint","INTERSECT",VERTEX,{"disambiguationData":[OD(0.0)],"derivedFrom":[subQ6,subQ5]});Q68=makeQuery(id+"F0.imprint","IMPRINT",FACE,{"disambiguationData":[TD([[makeQuery(id+"F0.imprint","IMPRINT",EDGE,{"disambiguationData":[TD([[subQ7,1.0]])],"derivedFrom":subQ6}),-1.0]])]});}
            extrude(context, id + "F1", {"entities" : qUnion([Q0, Q1, Q2, Q3, Q4, Q5, Q6, Q7, Q8, Q9, Q10, Q11, Q12, Q13, Q14, Q15, Q16, Q17, Q18, Q19, Q20, Q21, Q22, Q23, Q24, Q25, Q26, Q27, Q28, Q29, Q30, Q31, Q32, Q33, Q34, Q35, Q36, Q37, Q38, Q39, Q40, Q41, Q42, Q43, Q44, Q45, Q46, Q47, Q48, Q49, Q50, Q51, Q52, Q53, Q54, Q55, Q56, Q57, Q58, Q59, Q60, Q61, Q62, Q63, Q64, Q65, Q66, Q67, Q68]), "depth" : 3.5 * mm, "offsetDistance" : 25 * mm});
        }
        {
            var Q0;
            Q0=makeQuery(id+"F1.opExtrude","CAP_FACE",FACE,{"disambiguationData":[OSD([sQuery(id+"F0.wireOp",EDGE,"E0"),sQuery(id+"F0.wireOp",EDGE,"E3")])],"isStart":false});
            var sketch = newSketch(context, id + "F2", { "sketchPlane" : qUnion([Q0])});
            skCircle(sketch, "E17.0", {"center": v(0, 0) * mm, "radius": 39 * mm});
            skSolve(sketch);
        }
        {
            var Q0;
            Q0=makeQuery(id+"F2.imprint","IMPRINT",FACE,{"disambiguationData":[TD([[makeQuery(id+"F2.imprint","IMPRINT",EDGE,{"derivedFrom":sQuery(id+"F2.wireOp",EDGE,"E17.0")}),1.0]])]});
            extrude(context, id + "F3", {"entities" : qUnion([Q0]), "depth" : 1.5 * mm, "offsetDistance" : 25 * mm});
        }
        {
            var Q0;
            Q0=makeQuery(id+"F3.opExtrude","CAP_FACE",FACE,{"disambiguationData":[OSD([sQuery(id+"F0.wireOp",EDGE,"E3"),sQuery(id+"F2.wireOp",EDGE,"E17.0")])],"isStart":false});
            var sketch = newSketch(context, id + "F4", { "sketchPlane" : qUnion([Q0])});
            skCircle(sketch, "E18.0", {"center": v(0, 0) * mm, "radius": 43.5 * mm});
            skSolve(sketch);
        }
        {
            var Q0;
            Q0=makeQuery(id+"F4.imprint","IMPRINT",FACE,{"disambiguationData":[TD([[makeQuery(id+"F4.imprint","IMPRINT",EDGE,{"derivedFrom":sQuery(id+"F4.wireOp",EDGE,"E18.0")}),1.0]])]});
            var Q1;
            Q1=makeQuery(id+"F4.imprint","IMPRINT",FACE,{"disambiguationData":[TD([[makeQuery(id+"F4.imprint","IMPRINT",EDGE,{"derivedFrom":makeQuery(id+"F3.opExtrude","CAP_EDGE",EDGE,{"disambiguationData":[OSD([sQuery(id+"F2.wireOp",EDGE,"E17.0")])],"isStart":false})}),1.0]])]});
            extrude(context, id + "F5", {"entities" : qUnion([Q0, Q1]), "operationType" : NewBodyOperationType.ADD, "depth" : 3.5 * mm, "offsetDistance" : 25 * mm});
        }
        {
            var Q0;
            Q0=makeQuery(id+"F0.imprint","IMPRINT",FACE,{"disambiguationData":[TD([[makeQuery(id+"F0.imprint","IMPRINT",EDGE,{"derivedFrom":sQuery(id+"F0.wireOp",EDGE,"E2")}),-1.0]])]});
            var Q1;
            {var subQ0=sQuery(id+"F0.wireOp",EDGE,"E5");var subQ1=sQuery(id+"F0.wireOp",EDGE,"E3");var subQ2=makeQuery(id+"F0.imprint","INTERSECT",VERTEX,{"disambiguationData":[OD(1.0)],"derivedFrom":[subQ1,subQ0]});Q1=makeQuery(id+"F0.imprint","IMPRINT",FACE,{"disambiguationData":[TD([[makeQuery(id+"F0.imprint","IMPRINT",EDGE,{"disambiguationData":[TD([[subQ2,-1.0]])],"derivedFrom":subQ1}),1.0]])]});}
            var Q2;
            {var subQ0=sQuery(id+"F0.wireOp",EDGE,"f54aecad-8b98-43cd-b3f4-bd551124e2040.MirrorCS");var subQ1=sQuery(id+"F0.wireOp",EDGE,"E3");var subQ2=makeQuery(id+"F0.imprint","INTERSECT",VERTEX,{"disambiguationData":[OD(1.0)],"derivedFrom":[subQ1,subQ0]});Q2=makeQuery(id+"F0.imprint","IMPRINT",FACE,{"disambiguationData":[TD([[makeQuery(id+"F0.imprint","IMPRINT",EDGE,{"disambiguationData":[TD([[subQ2,-1.0]])],"derivedFrom":subQ1}),1.0]])]});}
            var Q3;
            {var subQ0=sQuery(id+"F0.wireOp",EDGE,"E7");var subQ1=sQuery(id+"F0.wireOp",EDGE,"E3");var subQ2=makeQuery(id+"F0.imprint","INTERSECT",VERTEX,{"disambiguationData":[OD(1.0)],"derivedFrom":[subQ1,subQ0]});Q3=makeQuery(id+"F0.imprint","IMPRINT",FACE,{"disambiguationData":[TD([[makeQuery(id+"F0.imprint","IMPRINT",EDGE,{"disambiguationData":[TD([[subQ2,-1.0]])],"derivedFrom":subQ1}),1.0]])]});}
            var Q4;
            {var subQ0=sQuery(id+"F0.wireOp",EDGE,"0fc9e538-063d-4069-807a-62193617adc70.MirrorCS");var subQ1=sQuery(id+"F0.wireOp",EDGE,"E3");var subQ2=makeQuery(id+"F0.imprint","INTERSECT",VERTEX,{"disambiguationData":[OD(1.0)],"derivedFrom":[subQ1,subQ0]});Q4=makeQuery(id+"F0.imprint","IMPRINT",FACE,{"disambiguationData":[TD([[makeQuery(id+"F0.imprint","IMPRINT",EDGE,{"disambiguationData":[TD([[subQ2,-1.0]])],"derivedFrom":subQ1}),1.0]])]});}
            var Q5;
            {var subQ0=sQuery(id+"F0.wireOp",EDGE,"E8");var subQ1=sQuery(id+"F0.wireOp",EDGE,"E3");var subQ2=makeQuery(id+"F0.imprint","INTERSECT",VERTEX,{"disambiguationData":[OD(1.0)],"derivedFrom":[subQ1,subQ0]});Q5=makeQuery(id+"F0.imprint","IMPRINT",FACE,{"disambiguationData":[TD([[makeQuery(id+"F0.imprint","IMPRINT",EDGE,{"disambiguationData":[TD([[subQ2,-1.0]])],"derivedFrom":subQ1}),1.0]])]});}
            var Q6;
            {var subQ0=sQuery(id+"F0.wireOp",EDGE,"E4");var subQ1=sQuery(id+"F0.wireOp",EDGE,"E3");var subQ2=makeQuery(id+"F0.imprint","INTERSECT",VERTEX,{"disambiguationData":[OD(0.0)],"derivedFrom":[subQ1,subQ0]});Q6=makeQuery(id+"F0.imprint","IMPRINT",FACE,{"disambiguationData":[TD([[makeQuery(id+"F0.imprint","IMPRINT",EDGE,{"disambiguationData":[TD([[subQ2,1.0]])],"derivedFrom":subQ1}),1.0]])]});}
            var Q7;
            {var subQ0=sQuery(id+"F0.wireOp",EDGE,"c9230b24-fb15-4a67-97de-4f06d66d76500.MirrorCS");var subQ1=sQuery(id+"F0.wireOp",EDGE,"E3");var subQ2=makeQuery(id+"F0.imprint","INTERSECT",VERTEX,{"disambiguationData":[OD(0.0)],"derivedFrom":[subQ1,subQ0]});Q7=makeQuery(id+"F0.imprint","IMPRINT",FACE,{"disambiguationData":[TD([[makeQuery(id+"F0.imprint","IMPRINT",EDGE,{"disambiguationData":[TD([[subQ2,1.0]])],"derivedFrom":subQ1}),1.0]])]});}
            var Q8;
            {var subQ0=sQuery(id+"F0.wireOp",EDGE,"c9230b24-fb15-4a67-97de-4f06d66d76500.MirrorCS");var subQ1=sQuery(id+"F0.wireOp",EDGE,"E3");var subQ2=makeQuery(id+"F0.imprint","INTERSECT",VERTEX,{"disambiguationData":[OD(0.0)],"derivedFrom":[subQ1,subQ0]});Q8=makeQuery(id+"F0.imprint","IMPRINT",FACE,{"disambiguationData":[TD([[makeQuery(id+"F0.imprint","IMPRINT",EDGE,{"disambiguationData":[TD([[subQ2,-1.0]])],"derivedFrom":subQ1}),1.0]])]});}
            var Q9;
            {var subQ0=sQuery(id+"F0.wireOp",EDGE,"E7");var subQ1=sQuery(id+"F0.wireOp",EDGE,"E3");var subQ2=makeQuery(id+"F0.imprint","INTERSECT",VERTEX,{"disambiguationData":[OD(0.0)],"derivedFrom":[subQ1,subQ0]});Q9=makeQuery(id+"F0.imprint","IMPRINT",FACE,{"disambiguationData":[TD([[makeQuery(id+"F0.imprint","IMPRINT",EDGE,{"disambiguationData":[TD([[subQ2,-1.0]])],"derivedFrom":subQ1}),1.0]])]});}
            var Q10;
            {var subQ0=sQuery(id+"F0.wireOp",EDGE,"X2wNwJQT-B4Tv-bB2O-wKaQ-eUmFgRdWR0iJ");var subQ1=sQuery(id+"F0.wireOp",EDGE,"E3");var subQ2=makeQuery(id+"F0.imprint","INTERSECT",VERTEX,{"disambiguationData":[OD(0.0)],"derivedFrom":[subQ1,subQ0]});Q10=makeQuery(id+"F0.imprint","IMPRINT",FACE,{"disambiguationData":[TD([[makeQuery(id+"F0.imprint","IMPRINT",EDGE,{"disambiguationData":[TD([[subQ2,-1.0]])],"derivedFrom":subQ1}),1.0]])]});}
            var Q11;
            {var subQ0=sQuery(id+"F0.wireOp",EDGE,"E12");var subQ1=sQuery(id+"F0.wireOp",EDGE,"E3");var subQ2=makeQuery(id+"F0.imprint","INTERSECT",VERTEX,{"disambiguationData":[OD(0.0)],"derivedFrom":[subQ1,subQ0]});Q11=makeQuery(id+"F0.imprint","IMPRINT",FACE,{"disambiguationData":[TD([[makeQuery(id+"F0.imprint","IMPRINT",EDGE,{"disambiguationData":[TD([[subQ2,-1.0]])],"derivedFrom":subQ1}),1.0]])]});}
            var Q12;
            {var subQ0=sQuery(id+"F0.wireOp",EDGE,"Dt7iSOTS-iNF6-Fj9d-QwL8-E1cNRbcfdXUS");var subQ1=sQuery(id+"F0.wireOp",EDGE,"E3");var subQ2=makeQuery(id+"F0.imprint","INTERSECT",VERTEX,{"disambiguationData":[OD(0.0)],"derivedFrom":[subQ1,subQ0]});Q12=makeQuery(id+"F0.imprint","IMPRINT",FACE,{"disambiguationData":[TD([[makeQuery(id+"F0.imprint","IMPRINT",EDGE,{"disambiguationData":[TD([[subQ2,-1.0]])],"derivedFrom":subQ1}),1.0]])]});}
            var Q13;
            {var subQ0=sQuery(id+"F0.wireOp",EDGE,"E5");var subQ1=sQuery(id+"F0.wireOp",EDGE,"E3");var subQ2=makeQuery(id+"F0.imprint","INTERSECT",VERTEX,{"disambiguationData":[OD(0.0)],"derivedFrom":[subQ1,subQ0]});Q13=makeQuery(id+"F0.imprint","IMPRINT",FACE,{"disambiguationData":[TD([[makeQuery(id+"F0.imprint","IMPRINT",EDGE,{"disambiguationData":[TD([[subQ2,-1.0]])],"derivedFrom":subQ1}),1.0]])]});}
            var Q14;
            {var subQ0=sQuery(id+"F0.wireOp",EDGE,"f54aecad-8b98-43cd-b3f4-bd551124e2040.MirrorCS");var subQ1=sQuery(id+"F0.wireOp",EDGE,"E3");var subQ2=makeQuery(id+"F0.imprint","INTERSECT",VERTEX,{"disambiguationData":[OD(0.0)],"derivedFrom":[subQ1,subQ0]});Q14=makeQuery(id+"F0.imprint","IMPRINT",FACE,{"disambiguationData":[TD([[makeQuery(id+"F0.imprint","IMPRINT",EDGE,{"disambiguationData":[TD([[subQ2,-1.0]])],"derivedFrom":subQ1}),1.0]])]});}
            var Q15;
            {var subQ0=sQuery(id+"F0.wireOp",EDGE,"E10");var subQ1=sQuery(id+"F0.wireOp",EDGE,"E3");var subQ2=makeQuery(id+"F0.imprint","INTERSECT",VERTEX,{"disambiguationData":[OD(0.0)],"derivedFrom":[subQ1,subQ0]});Q15=makeQuery(id+"F0.imprint","IMPRINT",FACE,{"disambiguationData":[TD([[makeQuery(id+"F0.imprint","IMPRINT",EDGE,{"disambiguationData":[TD([[subQ2,-1.0]])],"derivedFrom":subQ1}),1.0]])]});}
            var Q16;
            {var subQ0=sQuery(id+"F0.wireOp",EDGE,"0fc9e538-063d-4069-807a-62193617adc70.MirrorCS");var subQ1=sQuery(id+"F0.wireOp",EDGE,"E3");var subQ2=makeQuery(id+"F0.imprint","INTERSECT",VERTEX,{"disambiguationData":[OD(0.0)],"derivedFrom":[subQ1,subQ0]});Q16=makeQuery(id+"F0.imprint","IMPRINT",FACE,{"disambiguationData":[TD([[makeQuery(id+"F0.imprint","IMPRINT",EDGE,{"disambiguationData":[TD([[subQ2,-1.0]])],"derivedFrom":subQ1}),1.0]])]});}
            var Q17;
            {var subQ0=sQuery(id+"F0.wireOp",EDGE,"E12");var subQ1=sQuery(id+"F0.wireOp",EDGE,"E3");var subQ2=makeQuery(id+"F0.imprint","INTERSECT",VERTEX,{"disambiguationData":[OD(1.0)],"derivedFrom":[subQ1,subQ0]});Q17=makeQuery(id+"F0.imprint","IMPRINT",FACE,{"disambiguationData":[TD([[makeQuery(id+"F0.imprint","IMPRINT",EDGE,{"disambiguationData":[TD([[subQ2,-1.0]])],"derivedFrom":subQ1}),1.0]])]});}
            var Q18;
            {var subQ0=sQuery(id+"F0.wireOp",EDGE,"f3349a83-585f-44af-833f-62577e2a71c40.MirrorCS");var subQ1=sQuery(id+"F0.wireOp",EDGE,"E3");var subQ2=makeQuery(id+"F0.imprint","INTERSECT",VERTEX,{"disambiguationData":[OD(0.0)],"derivedFrom":[subQ1,subQ0]});Q18=makeQuery(id+"F0.imprint","IMPRINT",FACE,{"disambiguationData":[TD([[makeQuery(id+"F0.imprint","IMPRINT",EDGE,{"disambiguationData":[TD([[subQ2,-1.0]])],"derivedFrom":subQ1}),1.0]])]});}
            var Q19;
            {var subQ0=sQuery(id+"F0.wireOp",EDGE,"E4");var subQ1=sQuery(id+"F0.wireOp",EDGE,"E3");var subQ2=makeQuery(id+"F0.imprint","INTERSECT",VERTEX,{"disambiguationData":[OD(1.0)],"derivedFrom":[subQ1,subQ0]});Q19=makeQuery(id+"F0.imprint","IMPRINT",FACE,{"disambiguationData":[TD([[makeQuery(id+"F0.imprint","IMPRINT",EDGE,{"disambiguationData":[TD([[subQ2,-1.0]])],"derivedFrom":subQ1}),1.0]])]});}
            var Q20;
            {var subQ0=sQuery(id+"F0.wireOp",EDGE,"c9230b24-fb15-4a67-97de-4f06d66d76500.MirrorCS");var subQ1=sQuery(id+"F0.wireOp",EDGE,"E3");var subQ2=makeQuery(id+"F0.imprint","INTERSECT",VERTEX,{"disambiguationData":[OD(1.0)],"derivedFrom":[subQ1,subQ0]});Q20=makeQuery(id+"F0.imprint","IMPRINT",FACE,{"disambiguationData":[TD([[makeQuery(id+"F0.imprint","IMPRINT",EDGE,{"disambiguationData":[TD([[subQ2,-1.0]])],"derivedFrom":subQ1}),1.0]])]});}
            var Q21;
            {var subQ0=sQuery(id+"F0.wireOp",EDGE,"E8");var subQ1=sQuery(id+"F0.wireOp",EDGE,"E3");var subQ2=makeQuery(id+"F0.imprint","INTERSECT",VERTEX,{"disambiguationData":[OD(0.0)],"derivedFrom":[subQ1,subQ0]});Q21=makeQuery(id+"F0.imprint","IMPRINT",FACE,{"disambiguationData":[TD([[makeQuery(id+"F0.imprint","IMPRINT",EDGE,{"disambiguationData":[TD([[subQ2,-1.0]])],"derivedFrom":subQ1}),1.0]])]});}
            var Q22;
            {var subQ0=sQuery(id+"F0.wireOp",EDGE,"X2wNwJQT-B4Tv-bB2O-wKaQ-eUmFgRdWR0iJ");var subQ1=sQuery(id+"F0.wireOp",EDGE,"E3");var subQ2=makeQuery(id+"F0.imprint","INTERSECT",VERTEX,{"disambiguationData":[OD(1.0)],"derivedFrom":[subQ1,subQ0]});Q22=makeQuery(id+"F0.imprint","IMPRINT",FACE,{"disambiguationData":[TD([[makeQuery(id+"F0.imprint","IMPRINT",EDGE,{"disambiguationData":[TD([[subQ2,-1.0]])],"derivedFrom":subQ1}),1.0]])]});}
            var Q23;
            {var subQ0=sQuery(id+"F0.wireOp",EDGE,"E10");var subQ1=sQuery(id+"F0.wireOp",EDGE,"E3");var subQ2=makeQuery(id+"F0.imprint","INTERSECT",VERTEX,{"disambiguationData":[OD(1.0)],"derivedFrom":[subQ1,subQ0]});Q23=makeQuery(id+"F0.imprint","IMPRINT",FACE,{"disambiguationData":[TD([[makeQuery(id+"F0.imprint","IMPRINT",EDGE,{"disambiguationData":[TD([[subQ2,-1.0]])],"derivedFrom":subQ1}),1.0]])]});}
            var Q24;
            {var subQ0=sQuery(id+"F0.wireOp",EDGE,"Dt7iSOTS-iNF6-Fj9d-QwL8-E1cNRbcfdXUS");var subQ1=sQuery(id+"F0.wireOp",EDGE,"E3");var subQ2=makeQuery(id+"F0.imprint","INTERSECT",VERTEX,{"disambiguationData":[OD(1.0)],"derivedFrom":[subQ1,subQ0]});Q24=makeQuery(id+"F0.imprint","IMPRINT",FACE,{"disambiguationData":[TD([[makeQuery(id+"F0.imprint","IMPRINT",EDGE,{"disambiguationData":[TD([[subQ2,-1.0]])],"derivedFrom":subQ1}),1.0]])]});}
            var Q25;
            {var subQ0=sQuery(id+"F0.wireOp",EDGE,"E12");var subQ1=sQuery(id+"F0.wireOp",EDGE,"E3");var subQ2=makeQuery(id+"F0.imprint","INTERSECT",VERTEX,{"disambiguationData":[OD(0.0)],"derivedFrom":[subQ1,subQ0]});Q25=makeQuery(id+"F0.imprint","IMPRINT",FACE,{"disambiguationData":[TD([[makeQuery(id+"F0.imprint","IMPRINT",EDGE,{"disambiguationData":[TD([[subQ2,1.0]])],"derivedFrom":subQ1}),1.0]])]});}
            extrude(context, id + "F6", {"entities" : qUnion([Q0, Q1, Q2, Q3, Q4, Q5, Q6, Q7, Q8, Q9, Q10, Q11, Q12, Q13, Q14, Q15, Q16, Q17, Q18, Q19, Q20, Q21, Q22, Q23, Q24, Q25]), "operationType" : NewBodyOperationType.ADD, "depth" : 20 * mm, "offsetDistance" : 25 * mm});
        }
        {
            var Q0;
            Q0=qCreatedBy(makeId("Front.planeOp"),FACE);
            var sketch = newSketch(context, id + "F7", { "sketchPlane" : qUnion([Q0])});
            skCircle(sketch, "E19", {"center": v(0, 11.5) * mm, "radius": 1.55 * mm});
            skCircle(sketch, "E20", {"center": v(0, 17) * mm, "radius": 1.55 * mm});
            skSolve(sketch);
        }
        {
            var Q0;
            Q0=makeQuery(id+"F7.imprint","IMPRINT",FACE,{"disambiguationData":[TD([[makeQuery(id+"F7.imprint","IMPRINT",EDGE,{"derivedFrom":sQuery(id+"F7.wireOp",EDGE,"E20")}),1.0]])]});
            var Q1;
            Q1=makeQuery(id+"F7.imprint","IMPRINT",FACE,{"disambiguationData":[TD([[makeQuery(id+"F7.imprint","IMPRINT",EDGE,{"derivedFrom":sQuery(id+"F7.wireOp",EDGE,"E19")}),1.0]])]});
            extrude(context, id + "F8", {"entities" : qUnion([Q0, Q1]), "operationType" : NewBodyOperationType.REMOVE, "depth" : 25 * mm, "offsetDistance" : 25 * mm});
        }
        {
            var Q0;
            Q0=makeQuery(id+"F1.opExtrude","CAP_EDGE",EDGE,{"disambiguationData":[OSD([sQuery(id+"F0.wireOp",EDGE,"E0")])],"isStart":false});
            chamfer(context, id + "F9", {"entities" : qUnion([Q0]), "chamferType" : ChamferType.TWO_OFFSETS, "width1" : 2.5 * mm, "oppositeDirection" : true, "width2" : 4.5 * mm, "tangentPropagation" : true});
        }
        {
            var Q0;
            Q0=makeQuery(id+"F5.opExtrude","CAP_EDGE",EDGE,{"disambiguationData":[OSD([sQuery(id+"F4.wireOp",EDGE,"E18.0")])],"isStart":true});
            chamfer(context, id + "F10", {"entities" : qUnion([Q0]), "chamferType" : ChamferType.TWO_OFFSETS, "width1" : 2.5 * mm, "oppositeDirection" : false, "width2" : 4.5 * mm, "tangentPropagation" : true});
        }
    });
